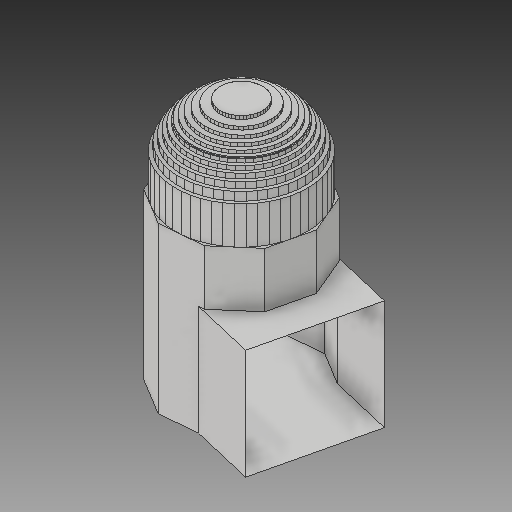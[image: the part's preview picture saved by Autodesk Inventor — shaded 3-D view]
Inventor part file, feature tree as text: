
AUTODESK INVENTOR PART (.ipt)
format: ipt  version: 2017 (Build 210142000, 142)  size: 1,773,056 bytes
history: native  units: in
note: dims shown in document units (in); Inventor stores cm internally (conversion verified against a paired STEP export)
features: extrude x10, sketch x7, other x3, plane x1, pattern_circular x1
ambient origin geometry x8: Origin, YZ Plane, XZ Plane, XY Plane, X Axis, Y Axis, Z Axis, Center Point
bodies: Solid1 (feature_tree)
feature tree (22):
  extrude  "bace"  Depth=1.0in TaperAngle=0.0deg
  extrude  "bace wall"  Depth=10.0in TaperAngle=0.0deg
  extrude  "bace ceiling"  Depth=6.6667in
  other  "used to find the workplane for the dome"
  plane  "workplane for dome"
  extrude  "dome make"  Depth=1.0in TaperAngle=0.0deg
  extrude  "dome part cut 1"  Depth=1.0in TaperAngle=0.0deg
  extrude  "dome part cut 2"  Depth=1.0in TaperAngle=360.0deg
  pattern_circular  "Circular Pattern6"  [2 undecoded]
  extrude  "door frame"  TaperAngle=45.0deg  [1 undecoded]
  extrude  "corridor connection"  Depth=0.1996in
  sketch  "Sketch19"  dims[d209=90.0deg d210=0.2in d214=45.0deg d223=0.1996in d224=0.1996in d225=0.1996in d226=0.1996in d227=0.1996in d228=0.1996in d229=0.1996in d230=0.1996in d231=0.1996in d232=0.1996in d233=0.1996in d234=0.1996in d235=1.0in d236=0.9303in d237=0.0in d238=0.9303in d239=0.0in]
  extrude  "extrusion to complete connection left"  Depth=0.1996in
  extrude  "extrusion to complete connection right"  Depth=0.1996in
  other  "Delete Faces of the room"
  other  "Delete Faces of dome"
  sketch  "Sketch1"  dims[d0=10.0in d1=1.0in d2=0.0in]
  sketch  "Sketch2"  dims[d4=1.0in d5=10.0in d6=0.0in]
  sketch  "Sketch3"  dims[d8=1.0in d9=0.0in d16=3.5in d17=6.6667in]
  sketch  "Sketch8"  dims[d18=3.0in d19=0.0in d107=1.0in d108=0.0in]
  sketch  "Sketch12"  dims[d186=4.1917in d187=0.0in d199=1.0in d200=0.0in]
  sketch  "Sketch17"  dims[d201=1.0in d202=0.0in d205=19.685in d206=360.0deg]
note: 3 required parameter values undecoded (feature->parameter linkage not recoverable at this tier; creation-order binding heuristic only, values carry confidence <= 0.55)
